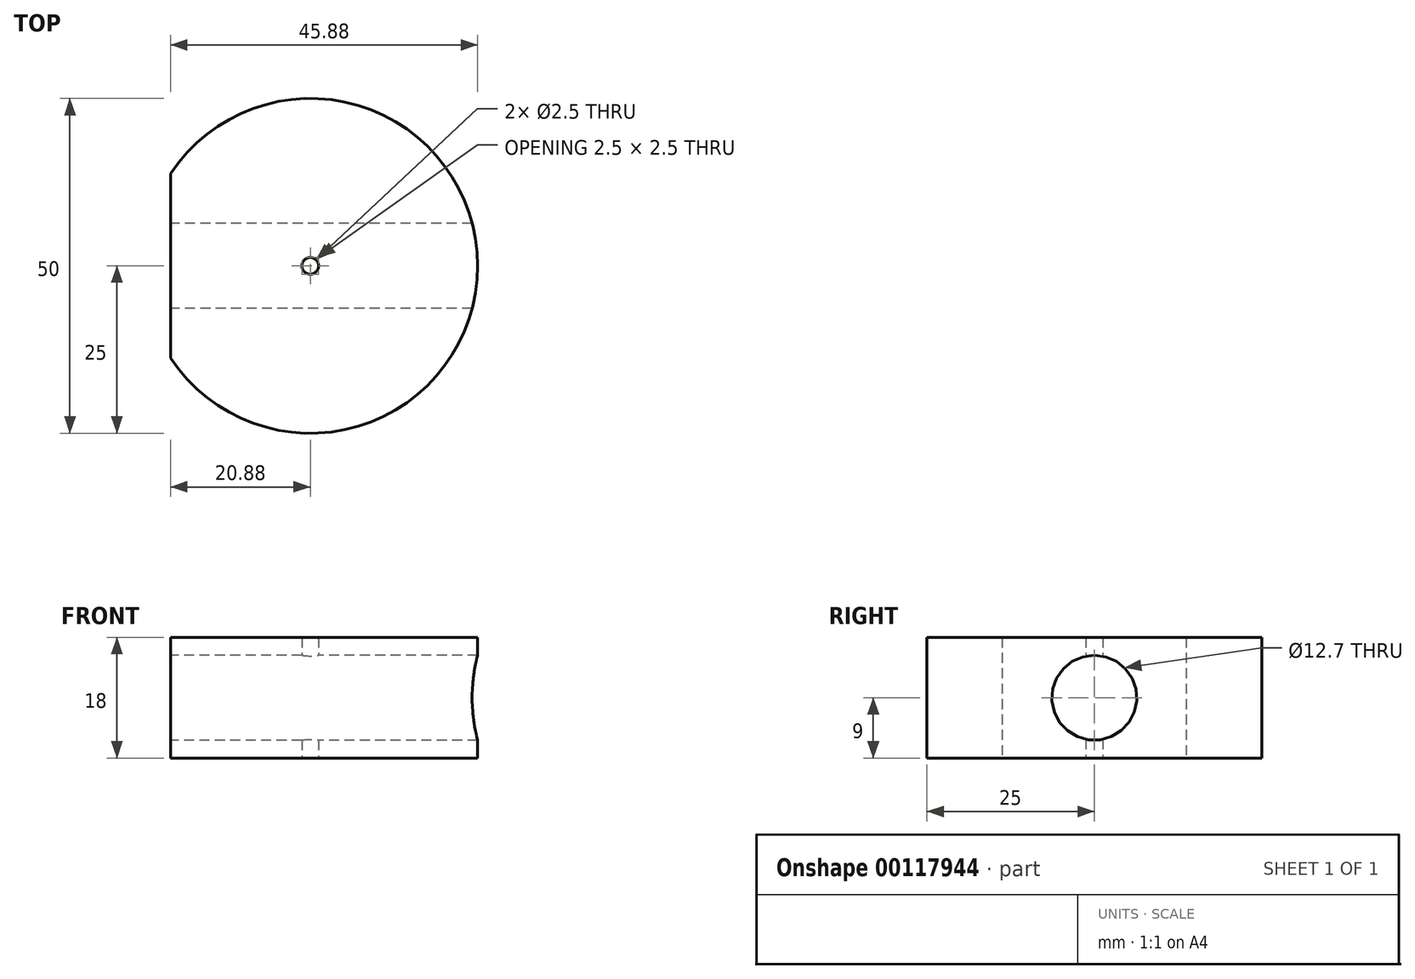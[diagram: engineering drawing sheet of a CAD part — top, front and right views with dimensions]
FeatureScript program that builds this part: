
annotation { "Feature Type Name" : "Feature", "Feature Type Description" : "" }
export const myFeature = defineFeature(function(context is Context, id is Id, definition is map)
    precondition{}
    {
        {
            var Q0;
            Q0=qCreatedBy(makeId("Top.planeOp"),FACE);
            var sketch = newSketch(context, id + "F0", { "sketchPlane" : qUnion([Q0])});
            skCircle(sketch, "E0", {"center": v(0, 0) * mm, "radius": 25 * mm});
            skCircle(sketch, "E1", {"center": v(0, 0) * mm, "radius": 1.25 * mm});
            skLineSegment(sketch, "E2", {"start": v(-20.88, 13.75) * mm, "end": v(-20.88, -13.75) * mm});
            skSolve(sketch);
        }
        {
            var Q0;
            Q0=makeQuery(id+"F0.imprint","IMPRINT",FACE,{"disambiguationData":[TD([[makeQuery(id+"F0.imprint","IMPRINT",EDGE,{"derivedFrom":sQuery(id+"F0.wireOp",EDGE,"E1")}),-1.0]])]});
            extrude(context, id + "F1", {"entities" : qUnion([Q0]), "depth" : 18 * mm});
        }
        {
            var Q0;
            Q0=makeQuery(id+"F1.opExtrude","SWEPT_FACE",FACE,{"disambiguationData":[OSD([sQuery(id+"F0.wireOp",EDGE,"E2")])]});
            var sketch = newSketch(context, id + "F2", { "sketchPlane" : qUnion([Q0])});
            skLineSegment(sketch, "E3", {"start": v(0, 0) * mm, "end": v(0, 18) * mm, "construction": true});
            skCircle(sketch, "E4", {"center": v(0, 9) * mm, "radius": 6.35 * mm});
            skSolve(sketch);
        }
        {
            var Q0;
            Q0=makeQuery(id+"F2.imprint","IMPRINT",FACE,{"disambiguationData":[TD([[makeQuery(id+"F2.imprint","IMPRINT",EDGE,{"derivedFrom":sQuery(id+"F2.wireOp",EDGE,"E4")}),1.0]])]});
            extrude(context, id + "F3", {"entities" : qUnion([Q0]), "operationType" : NewBodyOperationType.REMOVE, "oppositeDirection" : true, "depth" : 59.82 * mm});
        }
    });
